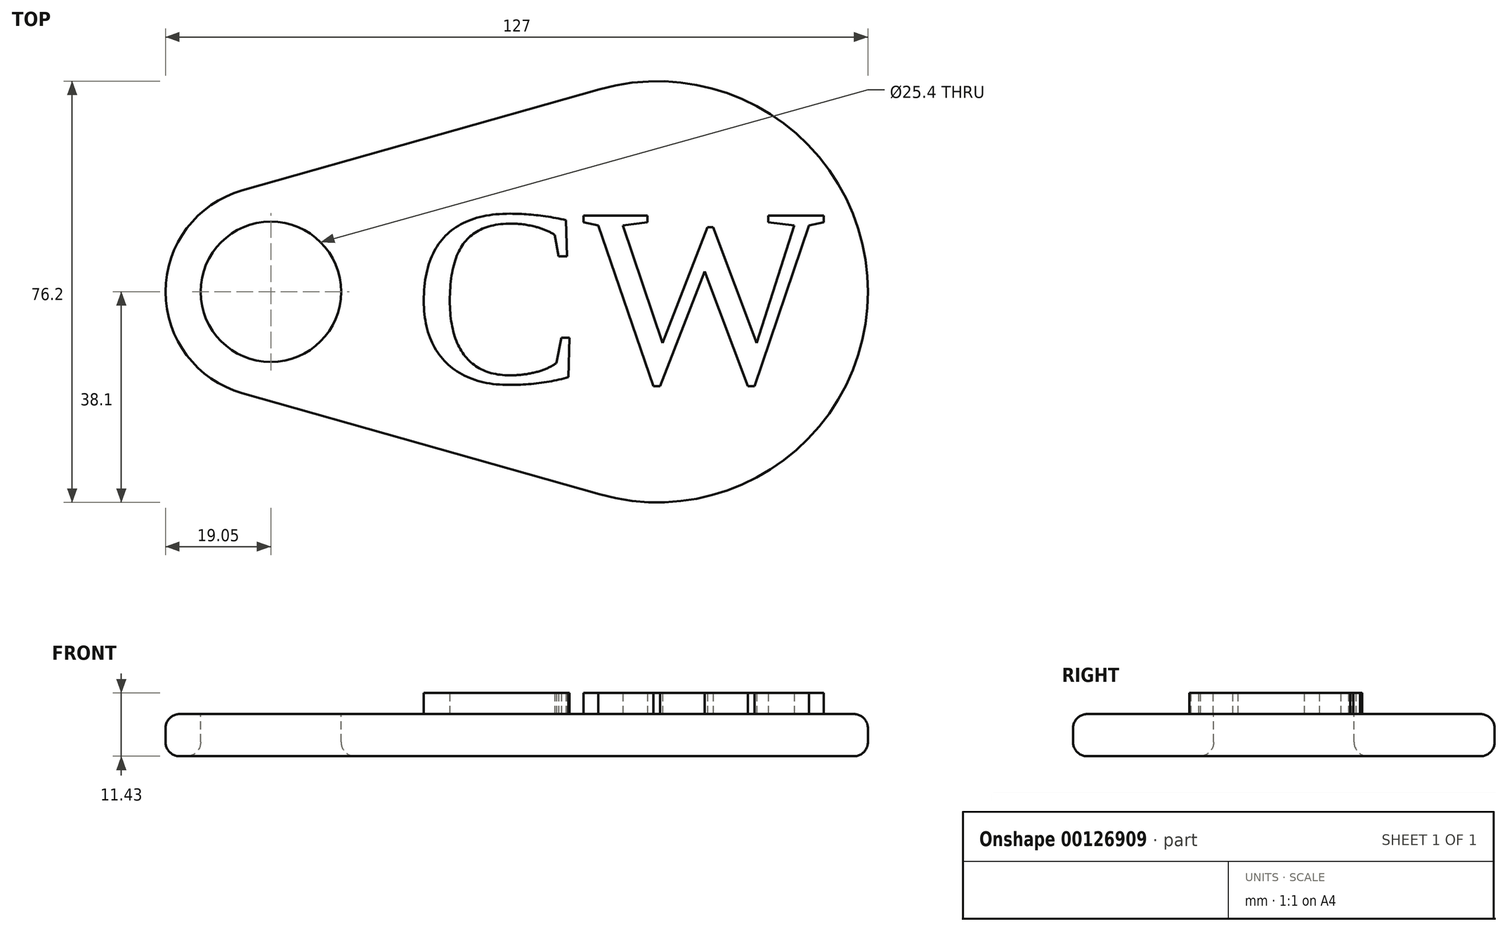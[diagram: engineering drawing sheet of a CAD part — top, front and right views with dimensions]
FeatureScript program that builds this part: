
annotation { "Feature Type Name" : "Feature", "Feature Type Description" : "" }
export const myFeature = defineFeature(function(context is Context, id is Id, definition is map)
    precondition{}
    {
        {
            var Q0;
            Q0=qCreatedBy(makeId("Top.planeOp"),FACE);
            var sketch = newSketch(context, id + "F0", { "sketchPlane" : qUnion([Q0])});
            skCircle(sketch, "E0", {"center": v(0, 0) * mm, "radius": 38.1 * mm});
            skCircle(sketch, "E1", {"center": v(-69.85, 0) * mm, "radius": 19.05 * mm});
            skLineSegment(sketch, "E2", {"start": v(-75.05, 18.33) * mm, "end": v(-10.4, 36.66) * mm});
            skLineSegment(sketch, "E3", {"start": v(-75.05, -18.33) * mm, "end": v(-10.4, -36.66) * mm});
            skSolve(sketch);
        }
        {
            var Q0;
            {var subQ0=sQuery(id+"F0.wireOp",EDGE,"E1");var subQ1=makeQuery(id+"F0.imprint","INTERSECT",VERTEX,{"derivedFrom":[subQ0,sQuery(id+"F0.wireOp",EDGE,"E2")]});Q0=makeQuery(id+"F0.imprint","IMPRINT",FACE,{"disambiguationData":[TD([[makeQuery(id+"F0.imprint","IMPRINT",EDGE,{"disambiguationData":[TD([[subQ1,-1.0]])],"derivedFrom":subQ0}),1.0]])]});}
            var Q1;
            {var subQ0=sQuery(id+"F0.wireOp",EDGE,"E2");Q1=makeQuery(id+"F0.imprint","IMPRINT",FACE,{"disambiguationData":[TD([[makeQuery(id+"F0.imprint","IMPRINT",EDGE,{"derivedFrom":subQ0}),-1.0]])]});}
            var Q2;
            {var subQ0=sQuery(id+"F0.wireOp",EDGE,"E0");var subQ1=makeQuery(id+"F0.imprint","INTERSECT",VERTEX,{"derivedFrom":[subQ0,sQuery(id+"F0.wireOp",EDGE,"E2")]});Q2=makeQuery(id+"F0.imprint","IMPRINT",FACE,{"disambiguationData":[TD([[makeQuery(id+"F0.imprint","IMPRINT",EDGE,{"disambiguationData":[TD([[subQ1,-1.0]])],"derivedFrom":subQ0}),1.0]])]});}
            extrude(context, id + "F1", {"entities" : qUnion([Q0, Q1, Q2]), "depth" : 7.62 * mm});
        }
        {
            var Q0;
            Q0=makeQuery(id+"F1.opExtrude","CAP_FACE",FACE,{"disambiguationData":[OSD([sQuery(id+"F0.wireOp",EDGE,"E0"),sQuery(id+"F0.wireOp",EDGE,"E1"),sQuery(id+"F0.wireOp",EDGE,"E2"),sQuery(id+"F0.wireOp",EDGE,"E3")])],"isStart":false});
            var sketch = newSketch(context, id + "F2", { "sketchPlane" : qUnion([Q0])});
            skText(sketch, "E4", { "text": "CW", "fontName": "Tinos-Regular.ttf"});
            const initialGuessF2  = {"E4": [-0.0441, -0.0164, 1, 0, 0.0332]};
            skSetInitialGuess(sketch, initialGuessF2);
            skSolve(sketch);
        }
        {
            var Q0;
            Q0=makeQuery(id+"F2.imprint","IMPRINT",FACE,{"disambiguationData":[TD([[makeQuery(id+"F2.imprint","IMPRINT",EDGE,{"derivedFrom":sQuery(id+"F2.wireOp",EDGE,"E4.sketch_text.stroke-0")}),1.0]])]});
            var sketch = newSketch(context, id + "F3", { "sketchPlane" : qUnion([Q0])});
            skCircle(sketch, "E5", {"center": v(-69.85, 0) * mm, "radius": 12.7 * mm});
            skSolve(sketch);
        }
        {
            var Q0;
            Q0=makeQuery(id+"F3.imprint","IMPRINT",FACE,{"disambiguationData":[TD([[makeQuery(id+"F3.imprint","IMPRINT",EDGE,{"derivedFrom":sQuery(id+"F3.wireOp",EDGE,"E5")}),1.0]])]});
            extrude(context, id + "F4", {"entities" : qUnion([Q0]), "operationType" : NewBodyOperationType.REMOVE, "oppositeDirection" : true, "depth" : 25.4 * mm});
        }
        {
            var Q0;
            Q0 = qSketchRegion(id + "F2", true);
            extrude(context, id + "F5", {"entities" : qUnion([Q0]), "operationType" : NewBodyOperationType.ADD, "depth" : 3.8 * mm});
        }
        {
            var Q0;
            Q0=makeQuery(id+"F4.boolean.opBoolean","COPY",EDGE,{"derivedFrom":makeQuery(id+"F4.opExtrude","CAP_EDGE",EDGE,{"disambiguationData":[OSD([sQuery(id+"F3.wireOp",EDGE,"E5")])],"isStart":true})});
            var Q1;
            Q1=makeQuery(id+"F1.opExtrude","CAP_EDGE",EDGE,{"disambiguationData":[OSD([sQuery(id+"F0.wireOp",EDGE,"E3")])],"isStart":false});
            var Q2;
            Q2=makeQuery(id+"F1.opExtrude","CAP_EDGE",EDGE,{"disambiguationData":[OSD([sQuery(id+"F0.wireOp",EDGE,"E0")])],"isStart":true});
            var Q3;
            Q3=makeQuery(id+"F4.boolean.opBoolean","INTERSECT",EDGE,{"derivedFrom":[makeQuery(id+"F1.opExtrude","CAP_FACE",FACE,{"disambiguationData":[OSD([sQuery(id+"F0.wireOp",EDGE,"E0"),sQuery(id+"F0.wireOp",EDGE,"E1"),sQuery(id+"F0.wireOp",EDGE,"E2"),sQuery(id+"F0.wireOp",EDGE,"E3")])],"isStart":true}),makeQuery(id+"F4.opExtrude","SWEPT_FACE",FACE,{"disambiguationData":[OSD([sQuery(id+"F3.wireOp",EDGE,"E5")])]})]});
            fillet(context, id + "F6", {"entities" : qUnion([Q0, Q1, Q2, Q3]), "radius" : 2.54 * mm, "tangentPropagation" : true, "allowEdgeOverflow" : false});
        }
    });
